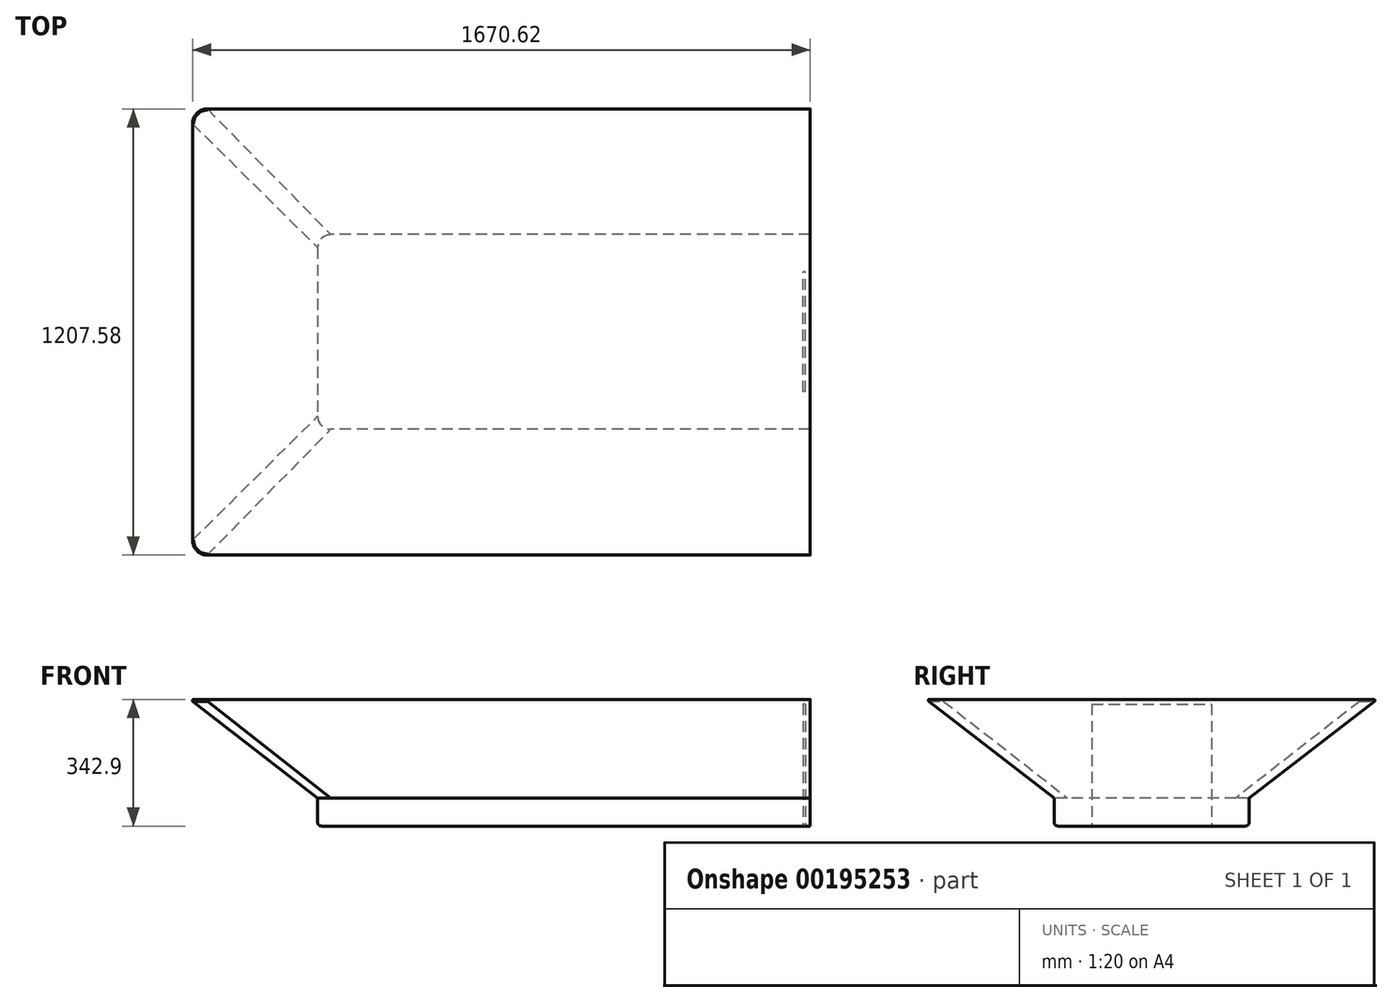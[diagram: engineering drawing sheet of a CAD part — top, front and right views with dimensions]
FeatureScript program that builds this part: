
annotation { "Feature Type Name" : "Feature", "Feature Type Description" : "" }
export const myFeature = defineFeature(function(context is Context, id is Id, definition is map)
    precondition{}
    {
        {
            var Q0;
            Q0=qCreatedBy(makeId("Top.planeOp"),FACE);
            cPlane(context, id + "F0", {"entities" : qUnion([Q0]), "cplaneType" : CPlaneType.OFFSET, "offset" : 266.7 * mm, "width" : 150 * mm, "height" : 150 * mm});
        }
        {
            var Q0;
            Q0=qCreatedBy(makeId("Top.planeOp"),FACE);
            cPlane(context, id + "F1", {"entities" : qUnion([Q0]), "cplaneType" : CPlaneType.OFFSET, "offset" : 76.2 * mm, "oppositeDirection" : true, "width" : 150 * mm, "height" : 150 * mm});
        }
        {
            var Q0;
            Q0=qCreatedBy(id+"F0.planeOp",FACE);
            var sketch = newSketch(context, id + "F2", { "sketchPlane" : qUnion([Q0])});
            skLineSegment(sketch, "E0.bottom", {"start": v(0, 609.6) * mm, "end": v(-1636.4, 609.6) * mm});
            skLineSegment(sketch, "E0.top", {"start": v(0, -609.6) * mm, "end": v(-1636.4, -609.6) * mm});
            skLineSegment(sketch, "E0.left", {"start": v(0, 609.6) * mm, "end": v(0, -609.6) * mm});
            skLineSegment(sketch, "E0.right", {"start": v(-1676.4, 569.6) * mm, "end": v(-1676.4, -569.6) * mm});
            skPoint(sketch, "E1.visualSharp", {"position": v(-1676.4, 609.6) * mm});
            skArc(sketch, "E1.filletArc", {"start": v(-1636.4, 609.6) * mm, "mid": v(-1664.68, 597.88) * mm, "end": v(-1676.4, 569.6) * mm});
            skPoint(sketch, "E2.visualSharp", {"position": v(-1676.4, -609.6) * mm});
            skArc(sketch, "E2.filletArc", {"start": v(-1676.4, -569.6) * mm, "mid": v(-1664.68, -597.88) * mm, "end": v(-1636.4, -609.6) * mm});
            skSolve(sketch);
        }
        {
            var Q0;
            Q0=qCreatedBy(makeId("Top.planeOp"),FACE);
            var sketch = newSketch(context, id + "F3", { "sketchPlane" : qUnion([Q0])});
            skLineSegment(sketch, "E3.bottom", {"start": v(0, 307.97) * mm, "end": v(-1296.37, 307.98) * mm, "construction": true});
            skLineSegment(sketch, "E3.top", {"start": v(0, -307.98) * mm, "end": v(-1296.37, -307.97) * mm, "construction": true});
            skLineSegment(sketch, "E3.left", {"start": v(0, 307.98) * mm, "end": v(0, -307.98) * mm, "construction": true});
            skLineSegment(sketch, "E3.right", {"start": v(-1376.36, 227.98) * mm, "end": v(-1376.36, -227.98) * mm, "construction": true});
            skPoint(sketch, "E4.visualSharp", {"position": v(-1376.37, 307.98) * mm});
            skArc(sketch, "E4.filletArc", {"start": v(-1296.37, 307.98) * mm, "mid": v(-1352.93, 284.54) * mm, "end": v(-1376.37, 227.98) * mm, "construction": true});
            skPoint(sketch, "E5.visualSharp", {"position": v(-1376.37, -307.97) * mm});
            skArc(sketch, "E5.filletArc", {"start": v(-1376.37, -227.98) * mm, "mid": v(-1352.93, -284.54) * mm, "end": v(-1296.37, -307.98) * mm, "construction": true});
            skLineSegment(sketch, "E6.0", {"start": v(0, -263.53) * mm, "end": v(-1296.37, -263.52) * mm});
            skLineSegment(sketch, "E6.1", {"start": v(0, 263.52) * mm, "end": v(-1296.37, 263.53) * mm});
            skArc(sketch, "E6.2", {"start": v(-1296.37, 263.53) * mm, "mid": v(-1321.5, 253.11) * mm, "end": v(-1331.91, 227.97) * mm});
            skLineSegment(sketch, "E6.3", {"start": v(-1331.91, 227.97) * mm, "end": v(-1331.91, -227.97) * mm});
            skArc(sketch, "E6.4", {"start": v(-1331.91, -227.97) * mm, "mid": v(-1321.5, -253.11) * mm, "end": v(-1296.37, -263.53) * mm});
            skLineSegment(sketch, "E7", {"start": v(0, 263.52) * mm, "end": v(0, -263.53) * mm});
            skSolve(sketch);
        }
        {
            var Q0;
            Q0 = qSketchRegion(id + "F2", true);
            var Q1;
            Q1 = qSketchRegion(id + "F3", true);
            loft(context, id + "F4", {"sheetProfilesArray" : [{ "sheetProfileEntities" : qUnion([Q0]) }, { "sheetProfileEntities" : qUnion([Q1]) }]});
        }
        {
            var Q0;
            Q0=makeQuery(id+"F4.opLoft","CAP_FACE",FACE,{"disambiguationData":[OSD([makeQuery(id+"F3.imprint","IMPRINT",FACE,{"disambiguationData":[TD([[makeQuery(id+"F3.imprint","IMPRINT",EDGE,{"derivedFrom":sQuery(id+"F3.wireOp",EDGE,"E6.0")}),-1.0]])]})])],"isStart":true});
            extrude(context, id + "F5", {"entities" : qUnion([Q0]), "operationType" : NewBodyOperationType.ADD, "depth" : 76.2 * mm});
        }
        {
            var Q0;
            Q0=qCreatedBy(id+"F1.planeOp",FACE);
            var sketch = newSketch(context, id + "F6", { "sketchPlane" : qUnion([Q0])});
            skLineSegment(sketch, "E8", {"start": v(0, 0) * mm, "end": v(-12.7, 0) * mm, "construction": true});
            skLineSegment(sketch, "E9.bottom", {"start": v(-12.7, -161.93) * mm, "end": v(-19.05, -161.93) * mm});
            skLineSegment(sketch, "E9.top", {"start": v(-12.7, 161.92) * mm, "end": v(-19.05, 161.92) * mm});
            skLineSegment(sketch, "E9.left", {"start": v(-12.7, -161.93) * mm, "end": v(-12.7, 161.92) * mm});
            skLineSegment(sketch, "E9.right", {"start": v(-19.05, -161.93) * mm, "end": v(-19.05, 161.92) * mm});
            skSolve(sketch);
        }
        {
            var Q0;
            Q0 = qSketchRegion(id + "F6", true);
            extrude(context, id + "F7", {"entities" : qUnion([Q0]), "operationType" : NewBodyOperationType.REMOVE, "depth" : 330.2 * mm});
        }
        {
            var Q0;
            Q0=makeQuery(id+"F4.opLoft","MID_CAP_EDGE",EDGE,{"disambiguationData":[OSD([sQuery(id+"F2.wireOp",EDGE,"E0.top"),sQuery(id+"F2.wireOp",EDGE,"E0.left"),sQuery(id+"F2.wireOp",EDGE,"E2.filletArc")])],"capPos":0.0});
            var Q1;
            Q1=makeQuery(id+"F4.opLoft","MID_CAP_EDGE",EDGE,{"disambiguationData":[OSD([sQuery(id+"F2.wireOp",EDGE,"E0.top"),sQuery(id+"F2.wireOp",EDGE,"E0.right"),sQuery(id+"F2.wireOp",EDGE,"E2.filletArc")])],"capPos":0.0});
            var Q2;
            Q2=makeQuery(id+"F4.opLoft","MID_CAP_EDGE",EDGE,{"disambiguationData":[OSD([sQuery(id+"F2.wireOp",EDGE,"E0.right"),sQuery(id+"F2.wireOp",EDGE,"E1.filletArc"),sQuery(id+"F2.wireOp",EDGE,"E2.filletArc")])],"capPos":0.0});
            var Q3;
            Q3=makeQuery(id+"F4.opLoft","MID_CAP_EDGE",EDGE,{"disambiguationData":[OSD([sQuery(id+"F2.wireOp",EDGE,"E0.bottom"),sQuery(id+"F2.wireOp",EDGE,"E0.left"),sQuery(id+"F2.wireOp",EDGE,"E1.filletArc")])],"capPos":0.0});
            var Q4;
            Q4=makeQuery(id+"F4.opLoft","MID_CAP_EDGE",EDGE,{"disambiguationData":[OSD([sQuery(id+"F2.wireOp",EDGE,"E0.bottom"),sQuery(id+"F2.wireOp",EDGE,"E0.right"),sQuery(id+"F2.wireOp",EDGE,"E1.filletArc")])],"capPos":0.0});
            fillet(context, id + "F8", {"entities" : qUnion([Q0, Q1, Q2, Q3, Q4]), "radius" : 3 * mm, "tangentPropagation" : true, "allowEdgeOverflow" : false});
        }
        {
            var Q0;
            Q0=makeQuery(id+"F5.opExtrude","CAP_EDGE",EDGE,{"disambiguationData":[OSD([sQuery(id+"F3.wireOp",EDGE,"E6.1"),sQuery(id+"F3.wireOp",EDGE,"E6.2"),sQuery(id+"F3.wireOp",EDGE,"E7")])],"isStart":false});
            var Q1;
            Q1=makeQuery(id+"F5.opExtrude","CAP_EDGE",EDGE,{"disambiguationData":[OSD([sQuery(id+"F3.wireOp",EDGE,"E6.1"),sQuery(id+"F3.wireOp",EDGE,"E6.2"),sQuery(id+"F3.wireOp",EDGE,"E6.3")])],"isStart":false});
            var Q2;
            Q2=makeQuery(id+"F5.opExtrude","CAP_EDGE",EDGE,{"disambiguationData":[OSD([sQuery(id+"F3.wireOp",EDGE,"E6.2"),sQuery(id+"F3.wireOp",EDGE,"E6.3"),sQuery(id+"F3.wireOp",EDGE,"E6.4")])],"isStart":false});
            var Q3;
            Q3=makeQuery(id+"F5.opExtrude","CAP_EDGE",EDGE,{"disambiguationData":[OSD([sQuery(id+"F3.wireOp",EDGE,"E6.0"),sQuery(id+"F3.wireOp",EDGE,"E6.3"),sQuery(id+"F3.wireOp",EDGE,"E6.4")])],"isStart":false});
            var Q4;
            Q4=makeQuery(id+"F5.opExtrude","CAP_EDGE",EDGE,{"disambiguationData":[OSD([sQuery(id+"F3.wireOp",EDGE,"E6.0"),sQuery(id+"F3.wireOp",EDGE,"E6.4"),sQuery(id+"F3.wireOp",EDGE,"E7")])],"isStart":false});
            fillet(context, id + "F9", {"entities" : qUnion([Q0, Q1, Q2, Q3, Q4]), "radius" : 10 * mm, "tangentPropagation" : true, "allowEdgeOverflow" : false});
        }
    });
